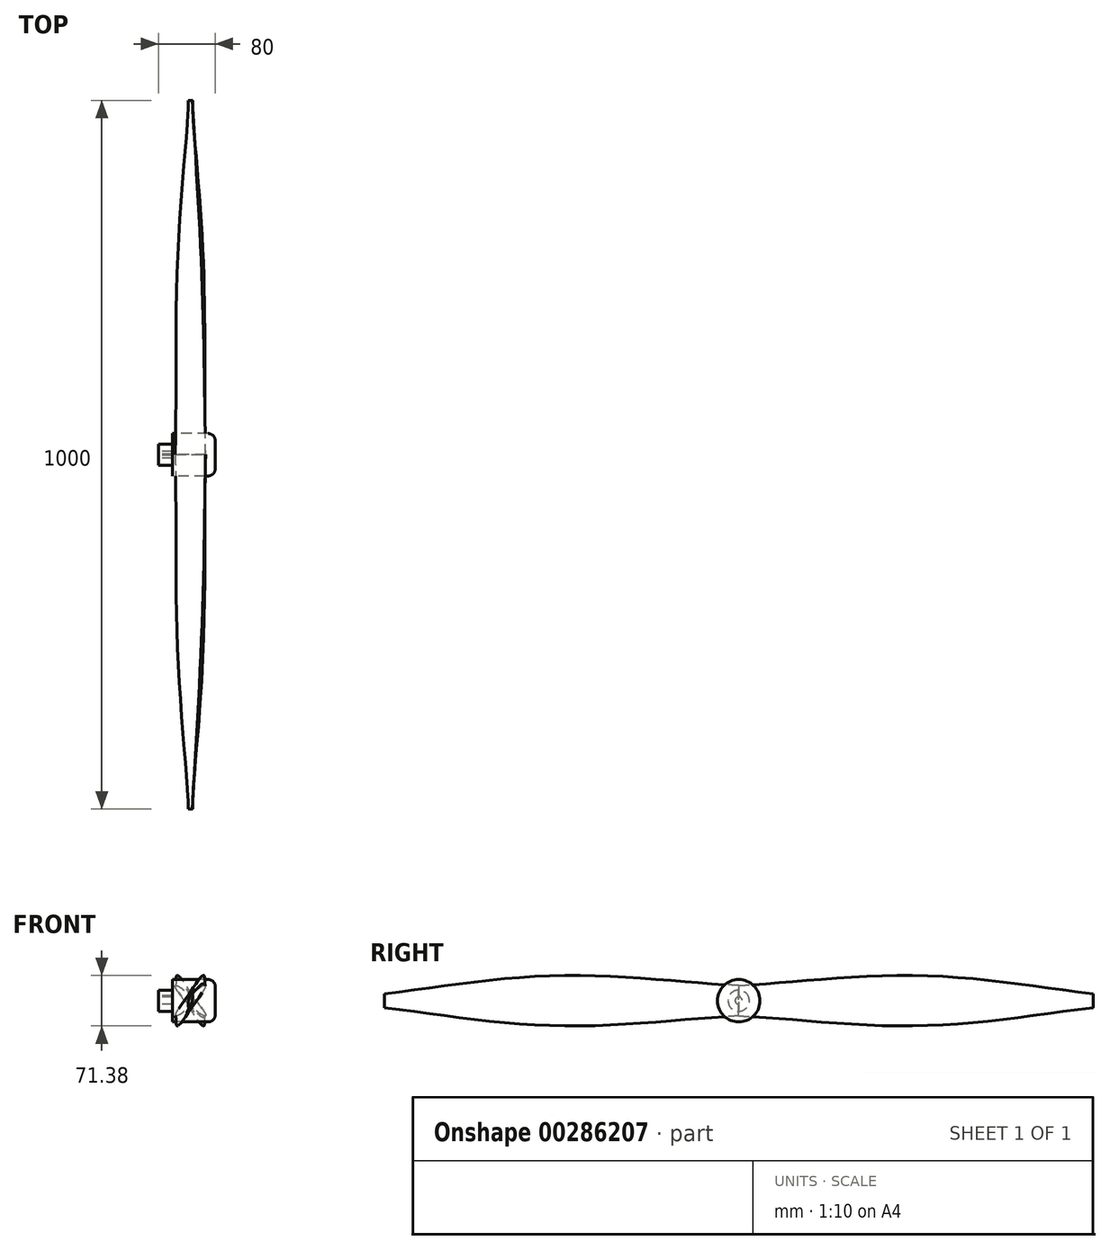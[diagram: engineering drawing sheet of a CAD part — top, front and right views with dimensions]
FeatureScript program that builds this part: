
annotation { "Feature Type Name" : "Feature", "Feature Type Description" : "" }
export const myFeature = defineFeature(function(context is Context, id is Id, definition is map)
    precondition{}
    {
        {
            var Q0;
            Q0=qCreatedBy(makeId("Front.planeOp"),FACE);
            var sketch = newSketch(context, id + "F0", { "sketchPlane" : qUnion([Q0])});
            skEllipse(sketch, "E0", {"center": v(0, 0) * mm, "majorRadius": 30 * mm, "minorRadius": 5 * mm, "majorAxis": v(0.7, 0.7)});
            skLineSegment(sketch, "E1", {"start": v(21.21, 21.21) * mm, "end": v(-21.21, -21.21) * mm, "construction": true});
            skLineSegment(sketch, "E2", {"start": v(-3.54, 3.54) * mm, "end": v(3.54, -3.54) * mm, "construction": true});
            skPoint(sketch, "E2.endSnap0", {"position": v(3.54, -3.54) * mm});
            skSolve(sketch);
        }
        {
            assignVariable(context, id + "F1", {"name" : "Amplitude", "anyValue" : 500});
        }
        {
            var Q0;
            Q0=qCreatedBy(makeId("Front.planeOp"),FACE);
            cPlane(context, id + "F2", {"entities" : qUnion([Q0]), "cplaneType" : CPlaneType.OFFSET, "offset" : (getVariable(context, 'Amplitude') / 2) * mm, "width" : 150 * mm, "height" : 150 * mm});
        }
        {
            var Q0;
            Q0=qCreatedBy(id+"F2.planeOp",FACE);
            var sketch = newSketch(context, id + "F3", { "sketchPlane" : qUnion([Q0])});
            skEllipse(sketch, "E3", {"center": v(0, 0) * mm, "majorRadius": 40 * mm, "minorRadius": 5 * mm, "majorAxis": v(-0.46, -0.89)});
            skLineSegment(sketch, "E4", {"start": v(18.47, 35.48) * mm, "end": v(-18.47, -35.48) * mm, "construction": true});
            skPoint(sketch, "E4.startSnap0", {"position": v(18.47, 35.48) * mm});
            skLineSegment(sketch, "E5", {"start": v(-4.44, 2.3) * mm, "end": v(4.44, -2.3) * mm, "construction": true});
            skSolve(sketch);
        }
        {
            var Q0;
            Q0=qCreatedBy(makeId("Front.planeOp"),FACE);
            cPlane(context, id + "F4", {"entities" : qUnion([Q0]), "cplaneType" : CPlaneType.OFFSET, "offset" : (getVariable(context, 'Amplitude')) * mm, "width" : 150 * mm, "height" : 150 * mm});
        }
        {
            var Q0;
            Q0=qCreatedBy(id+"F4.planeOp",FACE);
            var sketch = newSketch(context, id + "F5", { "sketchPlane" : qUnion([Q0])});
            skEllipse(sketch, "E6", {"center": v(0, 0) * mm, "majorRadius": 10.05 * mm, "minorRadius": 2.5 * mm, "majorAxis": v(0.2, 0.98)});
            skLineSegment(sketch, "E7", {"start": v(1.74, 9.85) * mm, "end": v(-1.74, -9.85) * mm, "construction": true});
            skPoint(sketch, "E7.startSnap0", {"position": v(2, 9.85) * mm});
            skPoint(sketch, "E7.endSnap0", {"position": v(-2, -9.85) * mm});
            skLineSegment(sketch, "E8", {"start": v(-2.45, 0.5) * mm, "end": v(2.45, -0.5) * mm, "construction": true});
            skSolve(sketch);
        }
        {
            var Q0;
            Q0=qSketchRegion(id+"F0",true);
            var Q1;
            Q1=qSketchRegion(id+"F3",true);
            var Q2;
            Q2=qSketchRegion(id+"F5",true);
            loft(context, id + "F6", {"sheetProfilesArray" : [{ "sheetProfileEntities" : qUnion([Q0]) }, { "sheetProfileEntities" : qUnion([Q1]) }, { "sheetProfileEntities" : qUnion([Q2]) }]});
        }
        {
            var Q0;
            Q0=qCreatedBy(makeId("Front.planeOp"),FACE);
            var sketch = newSketch(context, id + "F7", { "sketchPlane" : qUnion([Q0])});
            skLineSegment(sketch, "E9", {"start": v(-52.66, 0) * mm, "end": v(18.16, 0) * mm, "construction": true});
            skSolve(sketch);
        }
        {
            var Q0;
            Q0=makeQuery(id+"F6.opLoft","SWEPT_BODY",BODY,{"disambiguationData":[OSD([makeQuery(id+"F0.imprint","IMPRINT",FACE,{"disambiguationData":[TD([[makeQuery(id+"F0.imprint","IMPRINT",EDGE,{"derivedFrom":sQuery(id+"F0.wireOp",EDGE,"E0")}),1.0]])]}),sQuery(id+"F3.wireOp",EDGE,"E3"),makeQuery(id+"F5.imprint","IMPRINT",FACE,{"disambiguationData":[TD([[makeQuery(id+"F5.imprint","IMPRINT",EDGE,{"derivedFrom":sQuery(id+"F5.wireOp",EDGE,"E6")}),1.0]])]})])]});
            var Q1;
            Q1=sQuery(id+"F7.wireOp",EDGE,"E9");
            circularPattern(context, id + "F8", {"entities" : qUnion([Q0]), "axis" : qUnion([Q1]), "angle" : 180 * degree, "instanceCount" : 2});
        }
        {
            var Q0;
            Q0=qCreatedBy(makeId("Front.planeOp"),FACE);
            var sketch = newSketch(context, id + "F9", { "sketchPlane" : qUnion([Q0])});
            skLineSegment(sketch, "E10", {"start": v(-45, 0) * mm, "end": v(-45, 15) * mm});
            skLineSegment(sketch, "E11", {"start": v(-45, 15) * mm, "end": v(-25, 15) * mm});
            skLineSegment(sketch, "E12", {"start": v(-25, 15) * mm, "end": v(-25, 30) * mm});
            skLineSegment(sketch, "E13", {"start": v(-25, 30) * mm, "end": v(35, 30) * mm});
            skLineSegment(sketch, "E14", {"start": v(35, 30) * mm, "end": v(35, 0) * mm});
            skLineSegment(sketch, "E15", {"start": v(35, 0) * mm, "end": v(-45, 0) * mm});
            skLineSegment(sketch, "E16", {"start": v(-71.5, 0) * mm, "end": v(63.86, 0) * mm, "construction": true});
            skSolve(sketch);
        }
        {
            var Q0;
            Q0=qSketchRegion(id+"F9",true);
            var Q1;
            Q1=sQuery(id+"F9.wireOp",EDGE,"E16");
            revolve(context, id + "F10", {"entities" : qUnion([Q0]), "axis" : qUnion([Q1]), "revolveType" : RevolveType.FULL});
        }
        {
            var Q0;
            Q0=makeQuery(id+"F10.opRevolve","SWEPT_EDGE",EDGE,{"disambiguationData":[OSD([sQuery(id+"F9.wireOp",EDGE,"E13"),sQuery(id+"F9.wireOp",EDGE,"E14")])]});
            fillet(context, id + "F11", {"entities" : qUnion([Q0]), "radius" : 10 * mm, "tangentPropagation" : true, "allowEdgeOverflow" : false});
        }
        {
            var Q0;
            Q0=makeQuery(id+"F10.opRevolve","SWEPT_FACE",FACE,{"disambiguationData":[OSD([sQuery(id+"F9.wireOp",EDGE,"E10")])]});
            var sketch = newSketch(context, id + "F12", { "sketchPlane" : qUnion([Q0])});
            skArc(sketch, "E17", {"start": v(-1, 4.9) * mm, "mid": v(0, -5) * mm, "end": v(1, 4.9) * mm});
            skLineSegment(sketch, "E18.bottom", {"start": v(-1, 6.9) * mm, "end": v(1, 6.9) * mm});
            skLineSegment(sketch, "E18.left", {"start": v(-1, 6.9) * mm, "end": v(-1, 4.9) * mm});
            skLineSegment(sketch, "E18.right", {"start": v(1, 6.9) * mm, "end": v(1, 4.9) * mm});
            skSolve(sketch);
        }
        {
            var Q0;
            Q0=qSketchRegion(id+"F12",true);
            extrude(context, id + "F13", {"entities" : qUnion([Q0]), "operationType" : NewBodyOperationType.REMOVE, "oppositeDirection" : true, "depth" : 20 * mm});
        }
    });
